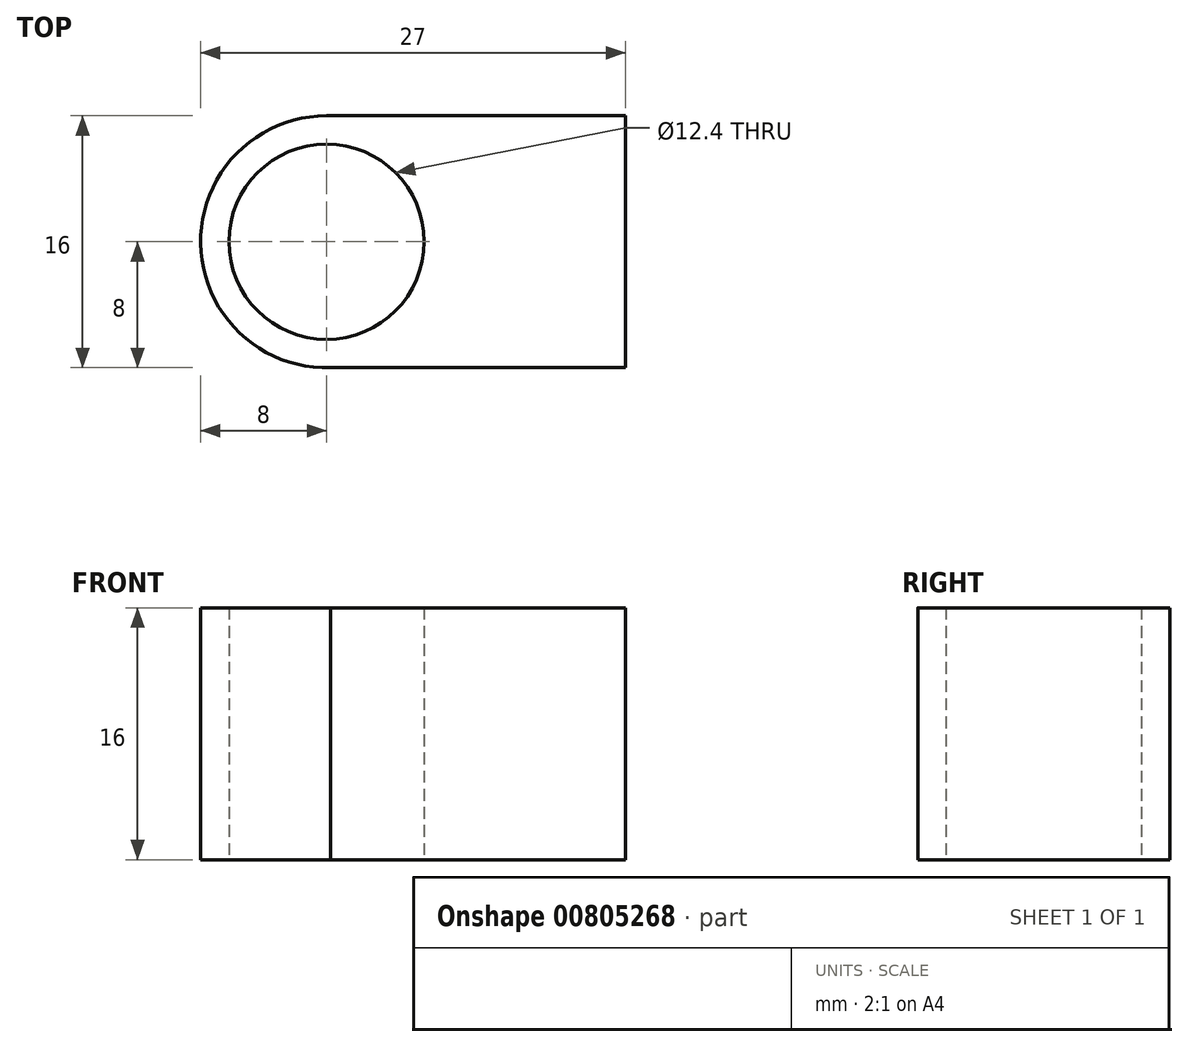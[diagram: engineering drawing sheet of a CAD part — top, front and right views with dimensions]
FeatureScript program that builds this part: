
annotation { "Feature Type Name" : "Feature", "Feature Type Description" : "" }
export const myFeature = defineFeature(function(context is Context, id is Id, definition is map)
    precondition{}
    {
        {
            var Q0;
            Q0=qCreatedBy(makeId("Top.planeOp"),FACE);
            var sketch = newSketch(context, id + "F0", { "sketchPlane" : qUnion([Q0])});
            skCircle(sketch, "E0", {"center": v(0, 0) * mm, "radius": 6.2 * mm});
            skCircle(sketch, "E1", {"center": v(0, 0) * mm, "radius": 8 * mm});
            skLineSegment(sketch, "E2.bottom", {"start": v(0, 8) * mm, "end": v(19, 8) * mm});
            skLineSegment(sketch, "E2.top", {"start": v(0, -8) * mm, "end": v(19, -8) * mm});
            skLineSegment(sketch, "E2.left", {"start": v(0, 8) * mm, "end": v(0, -8) * mm});
            skLineSegment(sketch, "E2.right", {"start": v(19, 8) * mm, "end": v(19, -8) * mm});
            skSolve(sketch);
        }
        {
            var Q0;
            {var subQ0=sQuery(id+"F0.wireOp",EDGE,"E2.left");var subQ3=sQuery(id+"F0.wireOp",EDGE,"E0");var subQ4=makeQuery(id+"F0.imprint","INTERSECT",VERTEX,{"disambiguationData":[OD(0.0)],"derivedFrom":[subQ3,subQ0]});Q0=makeQuery(id+"F0.imprint","IMPRINT",FACE,{"disambiguationData":[TD([[makeQuery(id+"F0.imprint","IMPRINT",EDGE,{"disambiguationData":[TD([[subQ4,1.0]])],"derivedFrom":subQ3}),-1.0]])]});}
            var Q1;
            {var subQ0=sQuery(id+"F0.wireOp",EDGE,"E2.left");var subQ3=sQuery(id+"F0.wireOp",EDGE,"E0");var subQ4=makeQuery(id+"F0.imprint","INTERSECT",VERTEX,{"disambiguationData":[OD(0.0)],"derivedFrom":[subQ3,subQ0]});Q1=makeQuery(id+"F0.imprint","IMPRINT",FACE,{"disambiguationData":[TD([[makeQuery(id+"F0.imprint","IMPRINT",EDGE,{"disambiguationData":[TD([[subQ4,-1.0]])],"derivedFrom":subQ3}),-1.0]])]});}
            var Q2;
            {var subQ0=sQuery(id+"F0.wireOp",EDGE,"E2.bottom");Q2=makeQuery(id+"F0.imprint","IMPRINT",FACE,{"disambiguationData":[TD([[makeQuery(id+"F0.imprint","IMPRINT",EDGE,{"derivedFrom":subQ0}),-1.0]])]});}
            extrude(context, id + "F1", {"entities" : qUnion([Q0, Q1, Q2]), "depth" : 16 * mm, "offsetDistance" : 25 * mm});
        }
    });
